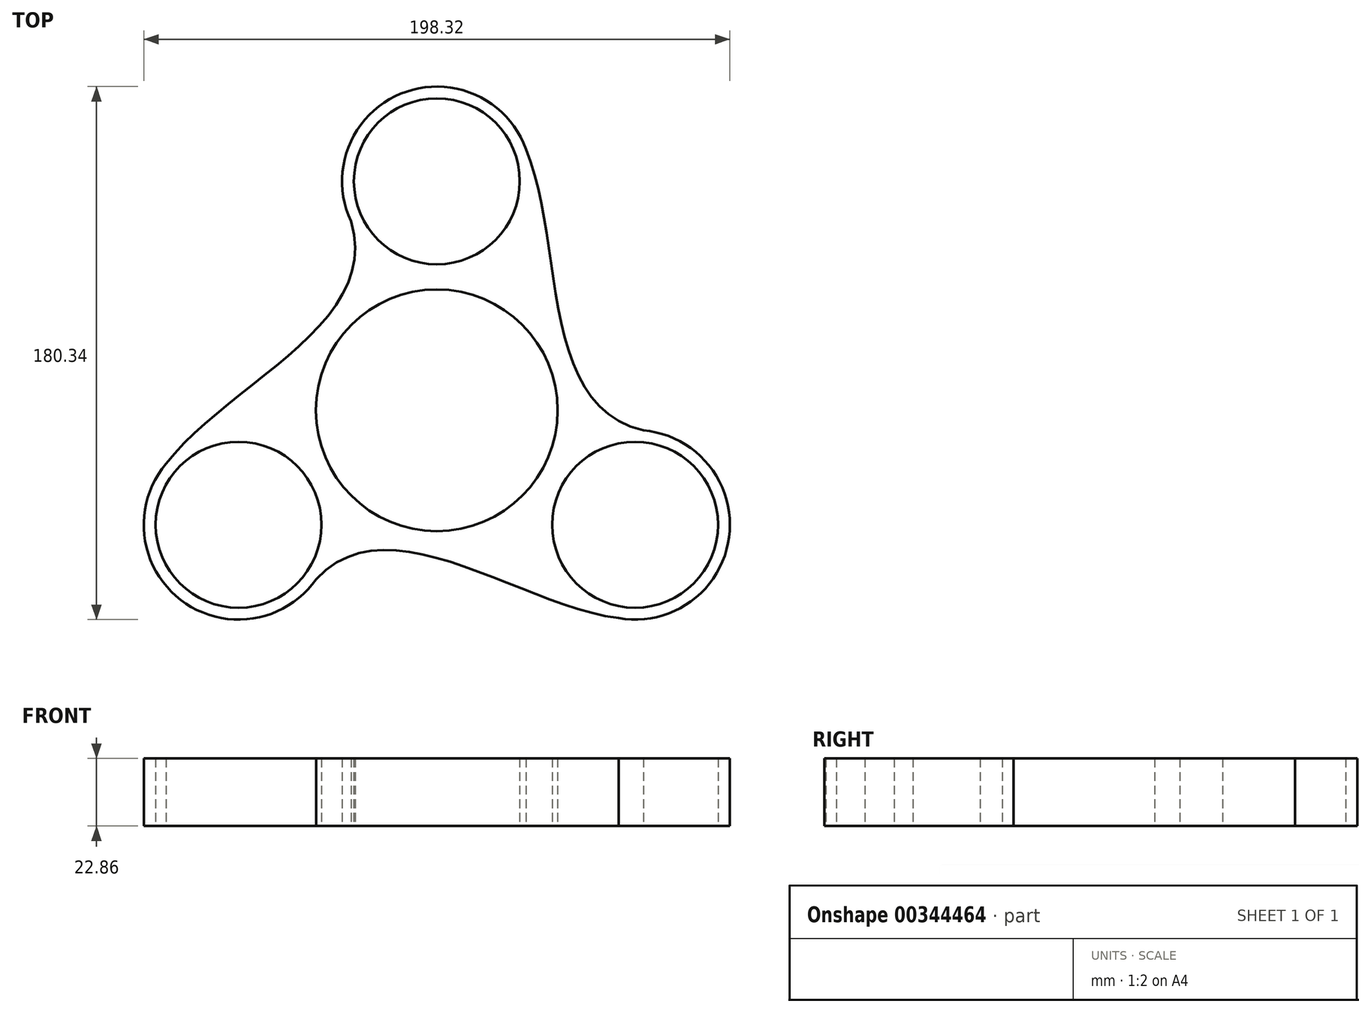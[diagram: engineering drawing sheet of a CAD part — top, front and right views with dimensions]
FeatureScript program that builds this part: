
annotation { "Feature Type Name" : "Feature", "Feature Type Description" : "" }
export const myFeature = defineFeature(function(context is Context, id is Id, definition is map)
    precondition{}
    {
        {
            var Q0;
            Q0=qCreatedBy(makeId("Top.planeOp"),FACE);
            var sketch = newSketch(context, id + "F0", { "sketchPlane" : qUnion([Q0])});
            skCircle(sketch, "E0", {"center": v(0.88, 0.46) * mm, "radius": 40.9 * mm});
            skCircle(sketch, "E1", {"center": v(-66.21, -38.27) * mm, "radius": 28.07 * mm});
            skCircle(sketch, "E2", {"center": v(67.97, -38.27) * mm, "radius": 28.07 * mm});
            skCircle(sketch, "E3", {"center": v(0.88, 77.93) * mm, "radius": 28.07 * mm});
            skCircle(sketch, "E4", {"center": v(-66.21, -38.27) * mm, "radius": 32.07 * mm});
            skCircle(sketch, "E5", {"center": v(0.88, 77.93) * mm, "radius": 32.07 * mm});
            skCircle(sketch, "E6", {"center": v(67.97, -38.27) * mm, "radius": 32.07 * mm});
            skFitSpline(sketch, "E7", {"points": [v(-28.2, 64.4) * mm, v(-90.77, -17.65) * mm], "startDerivative": vector(32.24, -104.89) * mm, "endDerivative": vector(-62.57, -82.06) * mm});
            skFitSpline(sketch, "E8", {"points": [v(70.8, -6.33) * mm, v(31.02, 88.9) * mm], "startDerivative": vector(-106.96, 24.52) * mm, "endDerivative": vector(-39.78, 95.22) * mm});
            skFitSpline(sketch, "E9", {"points": [v(-39.96, -56.69) * mm, v(62.39, -69.85) * mm], "startDerivative": vector(74.72, 80.37) * mm, "endDerivative": vector(102.35, -13.16) * mm});
            skSolve(sketch);
        }
        {
            var Q0;
            Q0 = qSketchRegion(id + "F0", true);
            extrude(context, id + "F1", {"entities" : qUnion([Q0]), "endBound" : BoundingType.SYMMETRIC, "depth" : 22.86 * mm});
        }
    });
